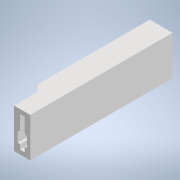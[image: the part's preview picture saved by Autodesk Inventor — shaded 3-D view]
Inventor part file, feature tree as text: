
AUTODESK INVENTOR PART (.ipt)
format: ipt  version: 2020 (Build 240168000, 168)  size: 160,256 bytes
history: native  units: mm
features: other x3, extrude x2, chamfer x2, sketch x2, thicken_offset x1, reference x1, projected_geometry x1
ambient origin geometry x8: Origin, YZ Plane, XZ Plane, XY Plane, X Axis, Y Axis, Z Axis, Center Point
bodies: Solid1 (feature_tree)
feature tree (12):
  extrude  "Extrusion1"  Depth=13.0mm
  extrude  "Extrusion2"  Depth=4.0mm
  chamfer  "Chamfer1"  Distance=2.0mm
  thicken_offset  "Thicken1"
  chamfer  "Chamfer2"  Distance=17.0mm
  sketch  "Sketch1"  dims[d0=2.0mm d1=13.0mm]
  reference  "Reference1"
  sketch  "Sketch2"  dims[d2=4.0mm d3=4.0mm d4=2.0mm d5=17.0mm d6=1.5mm d7=2.0mm d8=2.0mm d9=50.0mm d10=0.0mm d11=3.0mm d12=1.0mm d13=1.0mm d14=10.0mm d15=0.0mm d16=3.0mm d17=2.0mm d18=45.0deg d19=0.2mm d20=0.2mm d21=1.0mm d22=2.0mm d23=45.0deg]
  projected_geometry  "Projected Loop1"
  parser-record x1  (decoder bookkeeping rows leaked as tree rows — omitted from the tree; the rows remain in map.json)
  other  "motorized2.iam"
  other  "servo_bracket:1"
note: 1 file-system path scrubbed to <path> (originals preserved in map.json)
